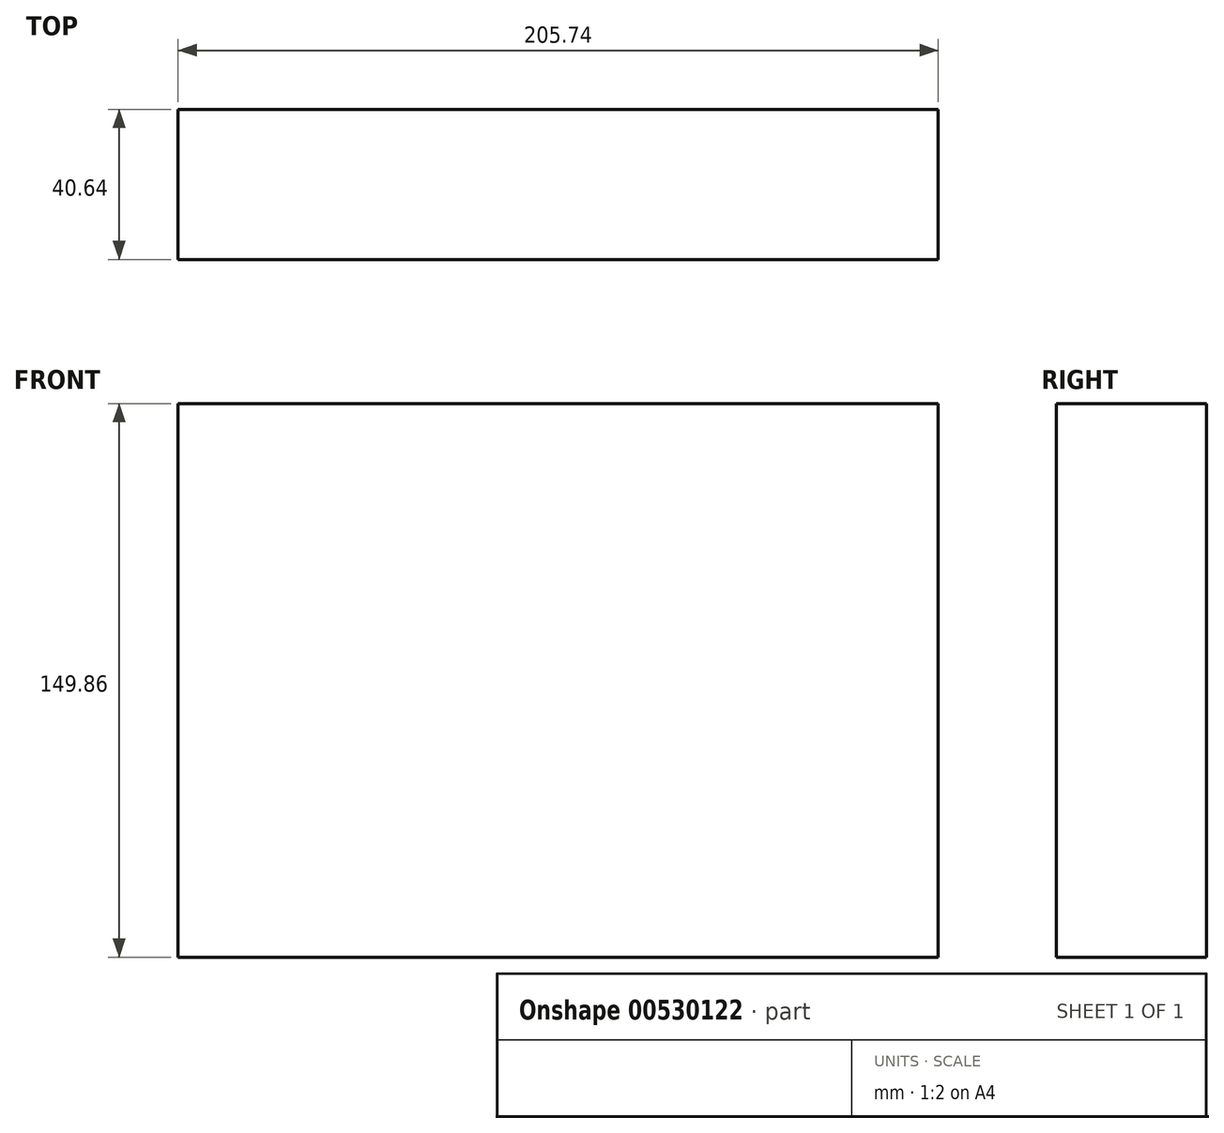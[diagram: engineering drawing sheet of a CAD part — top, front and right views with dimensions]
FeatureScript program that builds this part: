
annotation { "Feature Type Name" : "Feature", "Feature Type Description" : "" }
export const myFeature = defineFeature(function(context is Context, id is Id, definition is map)
    precondition{}
    {
        {
            var Q0;
            Q0=qCreatedBy(makeId("Front.planeOp"),FACE);
            var sketch = newSketch(context, id + "F0", { "sketchPlane" : qUnion([Q0])});
            skLineSegment(sketch, "E0.bottom", {"start": v(-102.87, 74.93) * mm, "end": v(102.87, 74.93) * mm});
            skLineSegment(sketch, "E0.top", {"start": v(-102.87, -74.93) * mm, "end": v(102.87, -74.93) * mm});
            skLineSegment(sketch, "E0.left", {"start": v(-102.87, 74.93) * mm, "end": v(-102.87, -74.93) * mm});
            skLineSegment(sketch, "E0.right", {"start": v(102.87, 74.93) * mm, "end": v(102.87, -74.93) * mm});
            skPoint(sketch, "E0.middle", {"position": v(0, 0) * mm});
            skSolve(sketch);
        }
        {
            var Q0;
            Q0 = qSketchRegion(id + "F0", true);
            extrude(context, id + "F1", {"entities" : qUnion([Q0]), "endBound" : BoundingType.SYMMETRIC, "depth" : 40.64 * mm, "offsetDistance" : 25.4 * mm});
        }
    });
